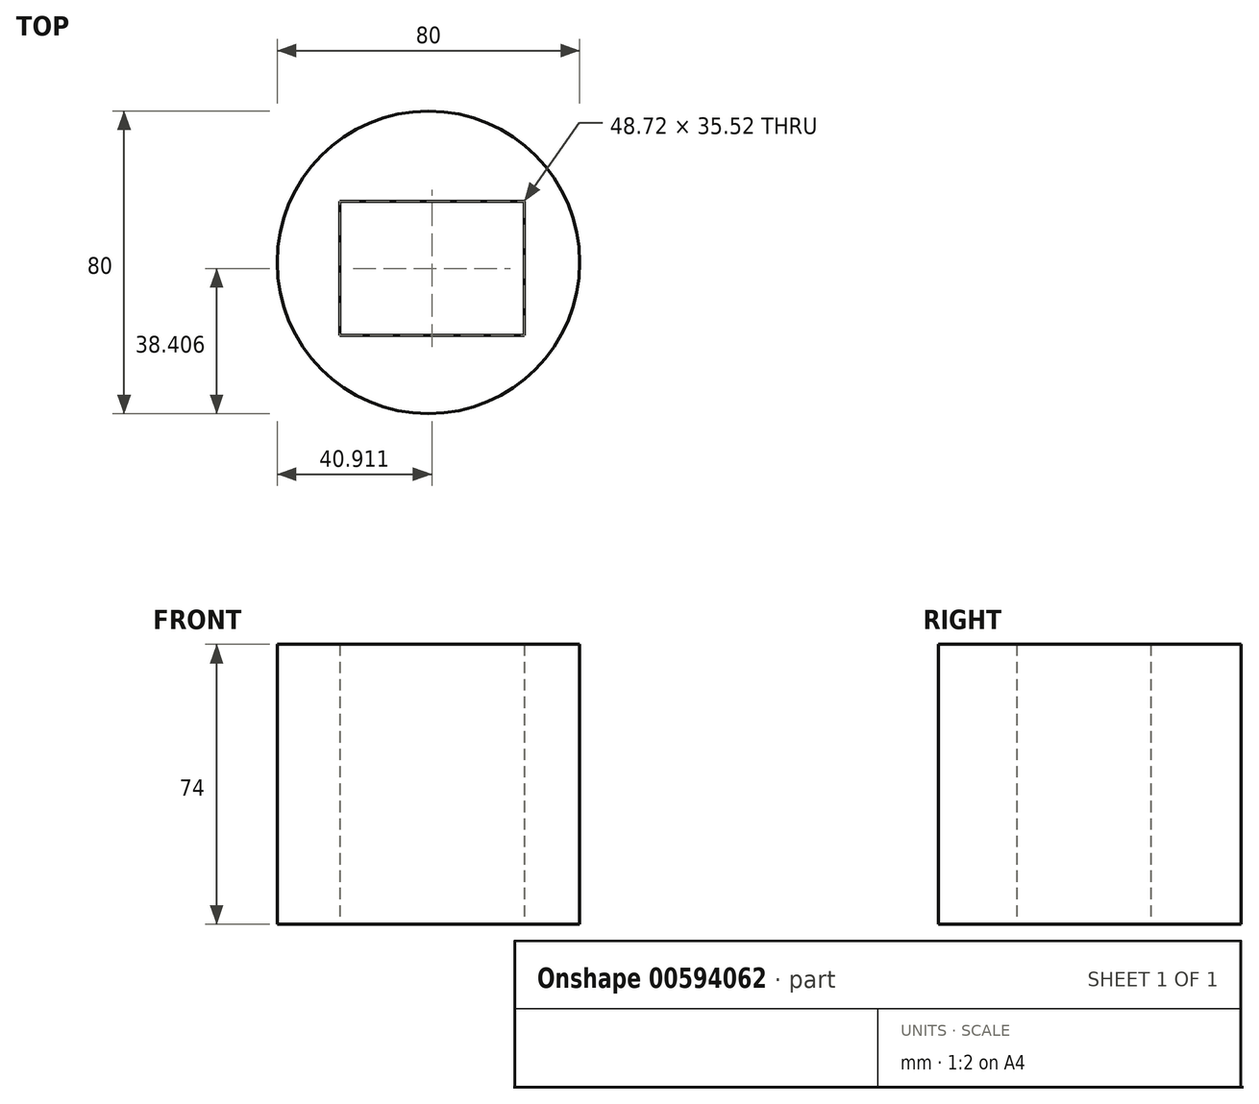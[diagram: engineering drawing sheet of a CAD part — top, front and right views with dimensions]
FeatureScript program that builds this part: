
annotation { "Feature Type Name" : "Feature", "Feature Type Description" : "" }
export const myFeature = defineFeature(function(context is Context, id is Id, definition is map)
    precondition{}
    {
        {
            var Q0;
            Q0=qCreatedBy(makeId("Top.planeOp"),FACE);
            var sketch = newSketch(context, id + "F0", { "sketchPlane" : qUnion([Q0])});
            skCircle(sketch, "E0", {"center": v(0, 0) * mm, "radius": 40 * mm});
            skLineSegment(sketch, "E1.bottom", {"start": v(-23.45, 16.17) * mm, "end": v(25.27, 16.17) * mm});
            skLineSegment(sketch, "E1.top", {"start": v(-23.45, -19.35) * mm, "end": v(25.27, -19.35) * mm});
            skLineSegment(sketch, "E1.left", {"start": v(-23.45, 16.17) * mm, "end": v(-23.45, -19.35) * mm});
            skLineSegment(sketch, "E1.right", {"start": v(25.27, 16.17) * mm, "end": v(25.27, -19.35) * mm});
            skSolve(sketch);
        }
        {
            var Q0;
            Q0 = qSketchRegion(id + "F0", true);
            extrude(context, id + "F1", {"entities" : qUnion([Q0]), "depth" : 74 * mm, "offsetDistance" : 25 * mm});
        }
    });
